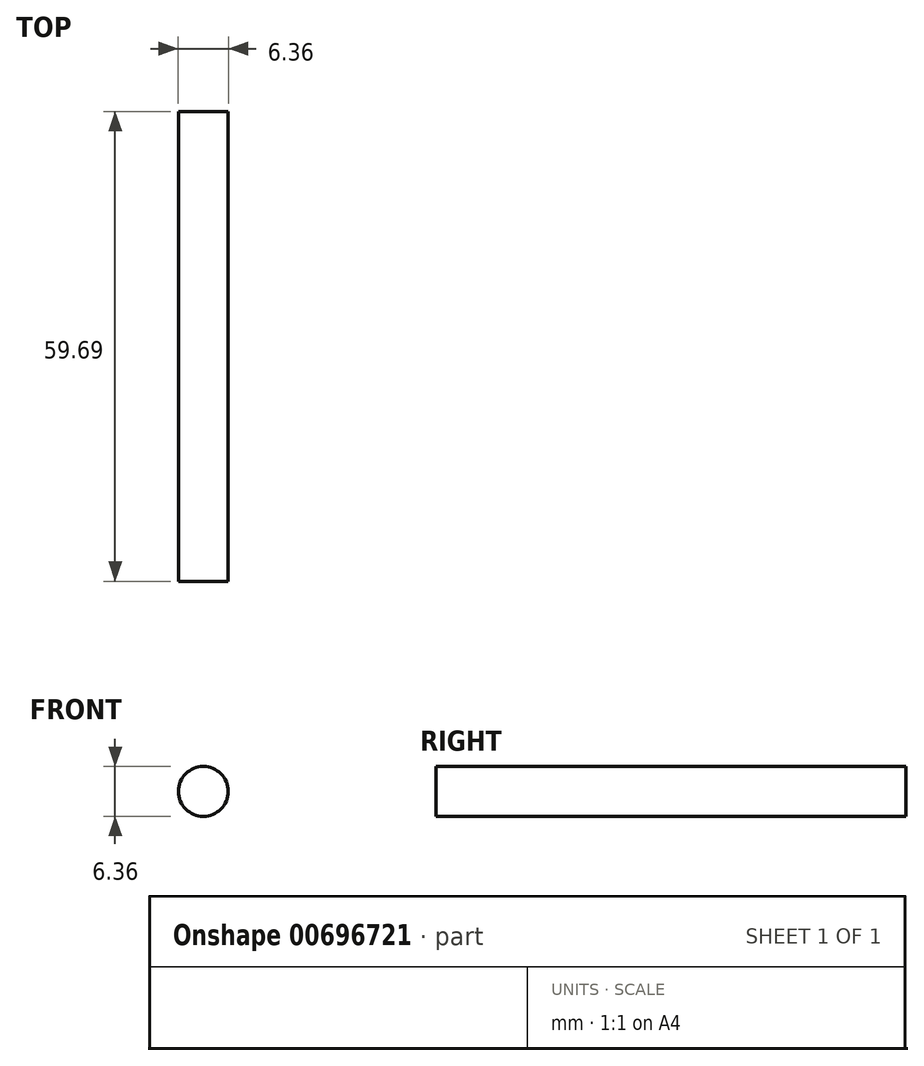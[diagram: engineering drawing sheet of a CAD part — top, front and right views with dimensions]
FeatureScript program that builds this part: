
annotation { "Feature Type Name" : "Feature", "Feature Type Description" : "" }
export const myFeature = defineFeature(function(context is Context, id is Id, definition is map)
    precondition{}
    {
        {
            var Q0;
            Q0=qCreatedBy(makeId("Front.planeOp"),FACE);
            var sketch = newSketch(context, id + "F0", { "sketchPlane" : qUnion([Q0])});
            skCircle(sketch, "E0", {"center": v(0, 0) * mm, "radius": 3.17 * mm});
            skSolve(sketch);
        }
        {
            var Q0;
            Q0=makeQuery(id+"F0.imprint","IMPRINT",FACE,{"disambiguationData":[TD([[makeQuery(id+"F0.imprint","IMPRINT",EDGE,{"derivedFrom":sQuery(id+"F0.wireOp",EDGE,"E0")}),1.0]])]});
            extrude(context, id + "F1", {"entities" : qUnion([Q0]), "depth" : 59.69 * mm, "offsetDistance" : 25.4 * mm});
        }
    });
